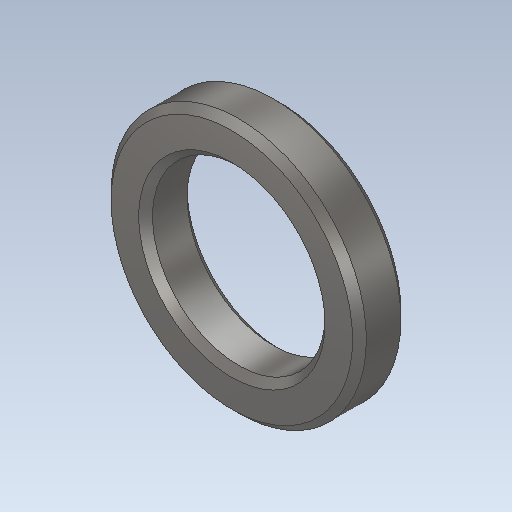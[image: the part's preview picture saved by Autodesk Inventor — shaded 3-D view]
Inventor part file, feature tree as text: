
AUTODESK INVENTOR PART (.ipt)
format: ipt  version: 2020 (Build 240168000, 168)  size: 132,608 bytes
history: native  units: mm
features: other x1, extrude x1, chamfer x1, sketch x1
ambient origin geometry x8: Origin, YZ Plane, XZ Plane, XY Plane, X Axis, Y Axis, Z Axis, Center Point
bodies: Body1 (feature_tree)
feature tree (4):
  other  "Bryła1"
  extrude  "Wyciągnięcie proste1"  Depth=25.0mm
  chamfer  "Faza1"  Distance=37.0mm
  sketch  "Szkic1"
